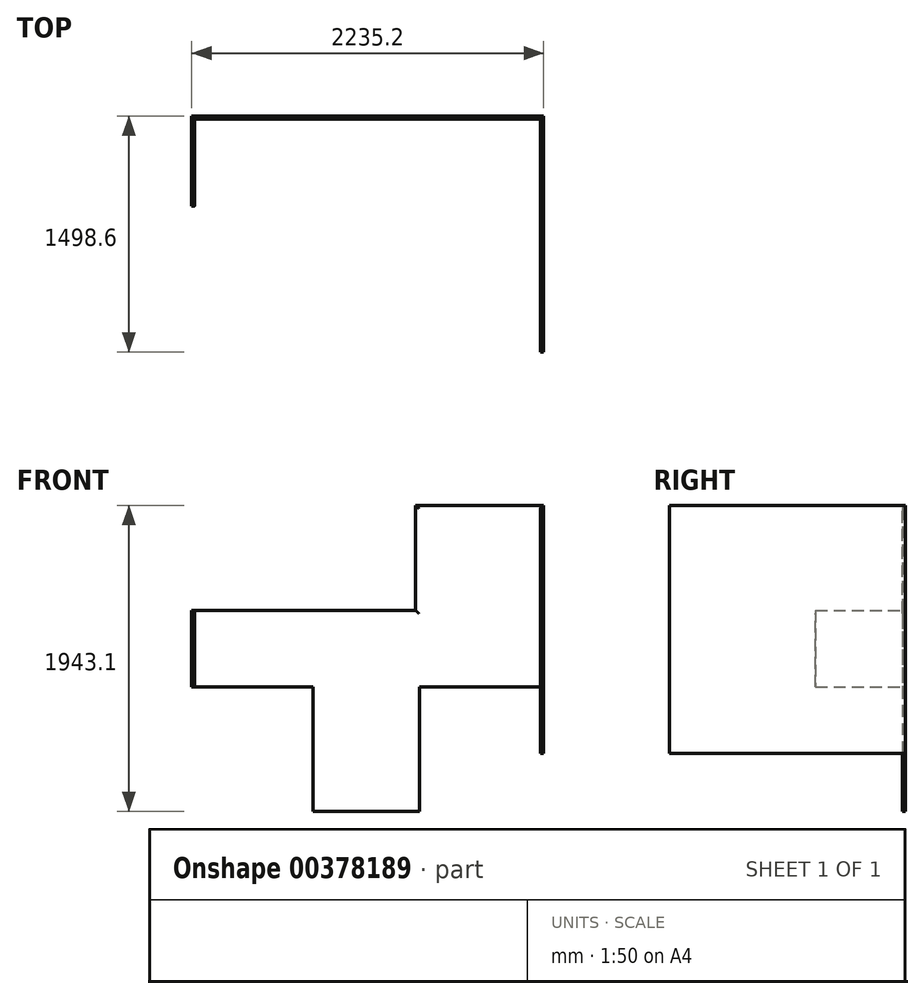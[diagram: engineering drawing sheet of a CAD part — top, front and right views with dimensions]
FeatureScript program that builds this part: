
annotation { "Feature Type Name" : "Feature", "Feature Type Description" : "" }
export const myFeature = defineFeature(function(context is Context, id is Id, definition is map)
    precondition{}
    {
        {
            var Q0;
            Q0=qCreatedBy(makeId("Front.planeOp"),FACE);
            var sketch = newSketch(context, id + "F0", { "sketchPlane" : qUnion([Q0])});
            skLineSegment(sketch, "E0.bottom", {"start": v(0, 0) * mm, "end": v(1422.4, 0) * mm});
            skLineSegment(sketch, "E0.top", {"start": v(0, -485.78) * mm, "end": v(1422.4, -485.78) * mm});
            skLineSegment(sketch, "E0.left", {"start": v(0, 0) * mm, "end": v(0, -485.78) * mm});
            skLineSegment(sketch, "E0.right", {"start": v(1422.4, 0) * mm, "end": v(1422.4, -485.78) * mm});
            skLineSegment(sketch, "E1.bottom", {"start": v(1422.4, -485.78) * mm, "end": v(2235.2, -485.78) * mm});
            skLineSegment(sketch, "E1.top", {"start": v(1422.4, 666.75) * mm, "end": v(2235.2, 666.75) * mm});
            skLineSegment(sketch, "E1.left", {"start": v(1422.4, -485.78) * mm, "end": v(1422.4, 666.75) * mm});
            skLineSegment(sketch, "E1.right", {"start": v(2235.2, -485.78) * mm, "end": v(2235.2, 666.75) * mm});
            skLineSegment(sketch, "E2.bottom", {"start": v(769.62, -485.78) * mm, "end": v(1447.8, -485.78) * mm});
            skLineSegment(sketch, "E2.top", {"start": v(769.62, -1276.35) * mm, "end": v(1447.8, -1276.35) * mm});
            skLineSegment(sketch, "E2.left", {"start": v(769.62, -485.78) * mm, "end": v(769.62, -1276.35) * mm});
            skLineSegment(sketch, "E2.right", {"start": v(1447.8, -485.78) * mm, "end": v(1447.8, -1276.35) * mm});
            skLineSegment(sketch, "E3.bottom", {"start": v(2235.2, -485.78) * mm, "end": v(1447.8, -485.78) * mm});
            skLineSegment(sketch, "E3.top", {"start": v(2235.2, -908.05) * mm, "end": v(1447.8, -908.05) * mm});
            skLineSegment(sketch, "E3.left", {"start": v(2235.2, -485.78) * mm, "end": v(2235.2, -908.05) * mm});
            skLineSegment(sketch, "E3.right", {"start": v(1447.8, -485.78) * mm, "end": v(1447.8, -908.05) * mm});
            skSolve(sketch);
        }
        {
            var Q0;
            {var subQ1=sQuery(id+"F0.wireOp",EDGE,"E0.bottom");Q0=makeQuery(id+"F0.imprint","IMPRINT",FACE,{"disambiguationData":[TD([[makeQuery(id+"F0.imprint","IMPRINT",EDGE,{"derivedFrom":subQ1}),-1.0]])]});}
            var Q1;
            Q1=makeQuery(id+"F0.imprint","IMPRINT",FACE,{"disambiguationData":[TD([[makeQuery(id+"F0.imprint","IMPRINT",EDGE,{"derivedFrom":sQuery(id+"F0.wireOp",EDGE,"E2.top")}),1.0]])]});
            var Q2;
            Q2=makeQuery(id+"F0.imprint","IMPRINT",FACE,{"disambiguationData":[TD([[makeQuery(id+"F0.imprint","IMPRINT",EDGE,{"derivedFrom":sQuery(id+"F0.wireOp",EDGE,"E3.bottom")}),1.0]])]});
            var Q3;
            {var subQ2=sQuery(id+"F0.wireOp",EDGE,"E1.top");Q3=makeQuery(id+"F0.imprint","IMPRINT",FACE,{"disambiguationData":[TD([[makeQuery(id+"F0.imprint","IMPRINT",EDGE,{"derivedFrom":subQ2}),-1.0]])]});}
            extrude(context, id + "F1", {"entities" : qUnion([Q0, Q1, Q2, Q3]), "depth" : 19.05 * mm});
        }
        {
            var Q0;
            Q0=makeQuery(id+"F1.opExtrude","CAP_FACE",FACE,{"disambiguationData":[OSD([sQuery(id+"F0.wireOp",EDGE,"E0.bottom"),sQuery(id+"F0.wireOp",EDGE,"E0.top"),sQuery(id+"F0.wireOp",EDGE,"E0.left"),sQuery(id+"F0.wireOp",EDGE,"E1.top"),sQuery(id+"F0.wireOp",EDGE,"E1.left"),sQuery(id+"F0.wireOp",EDGE,"E1.right"),sQuery(id+"F0.wireOp",EDGE,"E2.top"),sQuery(id+"F0.wireOp",EDGE,"E2.left"),sQuery(id+"F0.wireOp",EDGE,"E2.right"),sQuery(id+"F0.wireOp",EDGE,"E3.top"),sQuery(id+"F0.wireOp",EDGE,"E3.left")])],"isStart":true});
            var sketch = newSketch(context, id + "F2", { "sketchPlane" : qUnion([Q0])});
            skLineSegment(sketch, "E4.bottom", {"start": v(0, -485.78) * mm, "end": v(-19.05, -485.78) * mm});
            skLineSegment(sketch, "E4.top", {"start": v(0, 0) * mm, "end": v(-19.05, 0) * mm});
            skLineSegment(sketch, "E4.left", {"start": v(0, -485.78) * mm, "end": v(0, 0) * mm});
            skLineSegment(sketch, "E4.right", {"start": v(-19.05, -485.78) * mm, "end": v(-19.05, 0) * mm});
            skSolve(sketch);
        }
        {
            var Q0;
            Q0 = qSketchRegion(id + "F2", true);
            extrude(context, id + "F3", {"entities" : qUnion([Q0]), "operationType" : NewBodyOperationType.ADD, "oppositeDirection" : true, "depth" : 571.5 * mm});
        }
        {
            var Q0;
            Q0=makeQuery(id+"F1.opExtrude","CAP_FACE",FACE,{"disambiguationData":[OSD([sQuery(id+"F0.wireOp",EDGE,"E0.bottom"),sQuery(id+"F0.wireOp",EDGE,"E0.top"),sQuery(id+"F0.wireOp",EDGE,"E0.left"),sQuery(id+"F0.wireOp",EDGE,"E1.top"),sQuery(id+"F0.wireOp",EDGE,"E1.left"),sQuery(id+"F0.wireOp",EDGE,"E1.right"),sQuery(id+"F0.wireOp",EDGE,"E2.top"),sQuery(id+"F0.wireOp",EDGE,"E2.left"),sQuery(id+"F0.wireOp",EDGE,"E2.right"),sQuery(id+"F0.wireOp",EDGE,"E3.top"),sQuery(id+"F0.wireOp",EDGE,"E3.left")])],"isStart":true});
            var sketch = newSketch(context, id + "F4", { "sketchPlane" : qUnion([Q0])});
            skLineSegment(sketch, "E5.bottom", {"start": v(-2235.2, -908.05) * mm, "end": v(-2216.15, -908.05) * mm});
            skLineSegment(sketch, "E5.top", {"start": v(-2235.2, 666.75) * mm, "end": v(-2216.15, 666.75) * mm});
            skLineSegment(sketch, "E5.left", {"start": v(-2235.2, -908.05) * mm, "end": v(-2235.2, 666.75) * mm});
            skLineSegment(sketch, "E5.right", {"start": v(-2216.15, -908.05) * mm, "end": v(-2216.15, 666.75) * mm});
            skSolve(sketch);
        }
        {
            var Q0;
            Q0 = qSketchRegion(id + "F4", true);
            extrude(context, id + "F5", {"entities" : qUnion([Q0]), "operationType" : NewBodyOperationType.ADD, "oppositeDirection" : true, "depth" : 1498.6 * mm});
        }
        {
            var Q0;
            Q0=makeQuery(id+"F1.opExtrude","CAP_EDGE",EDGE,{"disambiguationData":[OSD([sQuery(id+"F0.wireOp",EDGE,"E0.bottom")])],"isStart":false});
            var Q1;
            Q1=makeQuery(id+"F1.opExtrude","CAP_EDGE",EDGE,{"disambiguationData":[OSD([sQuery(id+"F0.wireOp",EDGE,"E1.left")])],"isStart":false});
            var Q2;
            Q2=makeQuery(id+"F1.opExtrude","CAP_EDGE",EDGE,{"disambiguationData":[OSD([sQuery(id+"F0.wireOp",EDGE,"E1.top")])],"isStart":false});
            var Q3;
            Q3=makeQuery(id+"F3.opExtrude","SWEPT_EDGE",EDGE,{"disambiguationData":[OSD([sQuery(id+"F0.wireOp",EDGE,"E0.bottom"),sQuery(id+"F2.wireOp",EDGE,"E4.top"),sQuery(id+"F2.wireOp",EDGE,"E4.right")])]});
            var Q4;
            Q4=makeQuery(id+"F5.opExtrude","SWEPT_EDGE",EDGE,{"disambiguationData":[OSD([sQuery(id+"F0.wireOp",EDGE,"E1.top"),sQuery(id+"F4.wireOp",EDGE,"E5.top"),sQuery(id+"F4.wireOp",EDGE,"E5.right")])]});
            fillet(context, id + "F6", {"entities" : qUnion([Q0, Q1, Q2, Q3, Q4]), "radius" : 17.78 * mm, "tangentPropagation" : true, "allowEdgeOverflow" : false});
        }
    });
